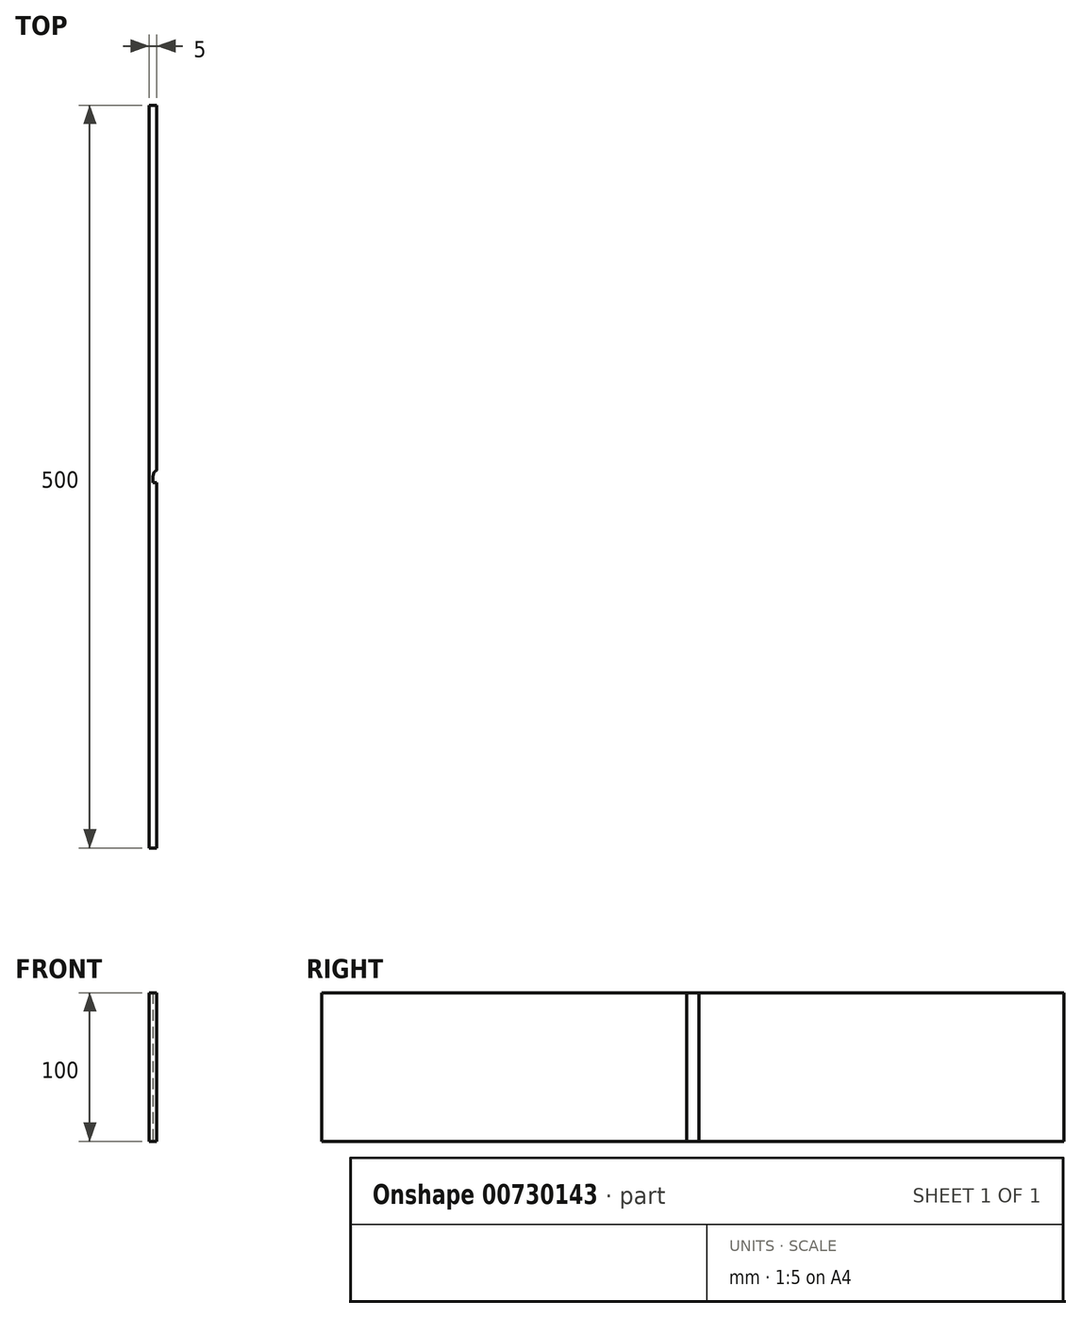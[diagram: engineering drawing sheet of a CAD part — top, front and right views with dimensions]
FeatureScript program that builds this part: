
annotation { "Feature Type Name" : "Feature", "Feature Type Description" : "" }
export const myFeature = defineFeature(function(context is Context, id is Id, definition is map)
    precondition{}
    {
        {
            assignVariable(context, id + "F0", {"name" : "h", "anyValue" : 100 * mm});
        }
        {
            var Q0;
            Q0=qCreatedBy(makeId("Top.planeOp"),FACE);
            var sketch = newSketch(context, id + "F1", { "sketchPlane" : qUnion([Q0])});
            skLineSegment(sketch, "E0.bottom", {"start": v(5, 250) * mm, "end": v(-5, 250) * mm});
            skLineSegment(sketch, "E0.top", {"start": v(5, -250) * mm, "end": v(-5, -250) * mm});
            skLineSegment(sketch, "E0.left", {"start": v(5, 250) * mm, "end": v(5, -250) * mm});
            skLineSegment(sketch, "E0.right", {"start": v(-5, 250) * mm, "end": v(-5, -250) * mm});
            skPoint(sketch, "E0.middle", {"position": v(0, 0) * mm});
            skLineSegment(sketch, "E1", {"start": v(0, 250) * mm, "end": v(0, -250) * mm});
            skEllipse(sketch, "E2", {"center": v(5, 0) * mm, "majorRadius": 4.04 * mm, "minorRadius": 2.5 * mm, "majorAxis": v(0, 1)});
            skLineSegment(sketch, "E3", {"start": v(2.5, 0) * mm, "end": v(2.5, -4.04) * mm});
            skLineSegment(sketch, "E4", {"start": v(5, -4.04) * mm, "end": v(2.5, -4.04) * mm});
            skPoint(sketch, "E5", {"position": v(7.5, 0) * mm});
            skPoint(sketch, "E6", {"position": v(5, 4.05) * mm});
            skSolve(sketch);
        }
        {
            var Q0;
            {var subQ8=sQuery(id+"F1.wireOp",EDGE,"E1");Q0=makeQuery(id+"F1.imprint","IMPRINT",FACE,{"disambiguationData":[TD([[makeQuery(id+"F1.imprint","IMPRINT",EDGE,{"derivedFrom":subQ8}),1.0]])]});}
            extrude(context, id + "F2", {"entities" : qUnion([Q0]), "depth" : getVariable(context, 'h'), "offsetDistance" : 25 * mm});
        }
    });
